# Revit family: Air_Conditioner_Packaged_Rooftop Z(T,V) 10-12.5T, Z(H,J,R,U,W,K, X(P,A) 12.5T
name_source: partatom
category: Mechanical Equipment
revit_build: Autodesk Revit 2018 (Build: 20170630_0700(x64)
units: mm (PartAtom-declared; Revit-internal decimal feet)

## family parameters
Always vertical = Yes
Cut with Voids When Loaded = No
Part Type = Normal
Room Calculation Point = No
Round Connector Dimension = Use Diameter
Shared = No
Work Plane-Based = No

## types (3) — shared parameters
Base Length = 89"
Cabinet Base Thickness = 3"
Clearance Back = 36"
Clearance Front = 36"
Clearance Left = 36"
Clearance Right = 12"
Clearance Top = 72"
Compressor Locked Rotor Current = 0 A
Compressor Maximum Continuous Current = 0 A
Compressor Quantity = 2
Compressor Running Load Current = 0 A
Compressor Size = 0
Compressor Type = Scroll
Condensate Drain Connection Diameter = 1"
Condensate Drain Connection Diameter (Side) = 1"
Condenser Fan Diameter = 24"
Condenser Fan Drive Type = Direct
Condenser Fan Full Load Current = 0 A
Condenser Fan HP = 0 VA
Condenser Fan Quantity = 4
Convenience Outlet Full Load Current = 0 A
Curb Length = 80 5/8"
Curb Material = Metal - JCI - Steel - Galvanized With Wood Nailer
Curb Thicknes = 2"
Curb Width = 50 1/2"
Description = Single Package Air Conditioners and Gas/Electric Heat Units - 12.5 Ton Unit
Evaporator Coil Fins per Inch = 15
Evaporator Coil Row Count = 4
Exhaust Air Flow = 0 CFM
Family Revision Date = 12/19/2017
Filter Size and Quantity = (24 x 20 x 2) - 4
Filter Type = 2"
Frame Finish = Paint - JCI - Powder Coated - Galvanized Steel
Gas Connection Diameter = 1"
Gas Connection Diameter (Side) = 1"
Gas Exhaust Vent Diameter = 3"
Gas Heating Performance MBH Input = 0 Btu/h
Gas Heating Performance MBH Output = 0 Btu/h
Grille Material = Metal - JCI - Steel - Galvanized - Screen
Height = 50 3/4"
Length = 119 1/2"
Manufacturer = Johnson Controls, Inc.
Maximum Overcurrent Protection = 0 A
Nominal Cooling Capacity = 12.5 ton
Number of Poles = 3
OmniClass Number = 23.75.10.24.21.27.14
OmniClass Title = Packaged Rooftop Air Conditioning Units
Power Factor = 1
Refrigerant Used = R-410A
Return Air Connection Height = 28"
Return Air Connection Height (Optional) = 28"
Return Air Connection Width = 18"
Return Air Connection Width (Optional) = 18"
Supply Air Connection Height = 24"
Supply Air Connection Height (Optional) = 18"
Supply Air Connection Width = 21"
Supply Air Connection Width (Optional) = 28"
Supply Fan Full Load Current = 0 A
Supply Fan HP = 0 VA
Type Comments = Predator Units
URL = www.johnsoncontrols.com
Voltage = 230 V
Width = 59"
zero-valued in all types: Energy Efficiency Rating, Integrated Part Load Value

## per-type parameters (varying)
| type | Condenser Coil Rows | Condenser Coils Fins per Inch | Model | Operating Weight | Refrigerant Charge System One | Refrigerant Charge System Two |
| ZH150 - 12.5 Ton | 1 | 23 | ZH150 | 1280.00 lb | 8.13 lb | 8.13 lb |
| ZJ150 - 12.5 Ton | 1 | 23 | ZJ150 | 1280.00 lb | 10.50 lb | 9.75 lb |
| ZR150 - 12.5 Ton | 2 | 15 | ZR150 | 1465.00 lb | 20.00 lb | 19.00 lb |

## geometry (parser evidence)
native form markers: Sweep x10
no freeform markers — native parametric forms only
